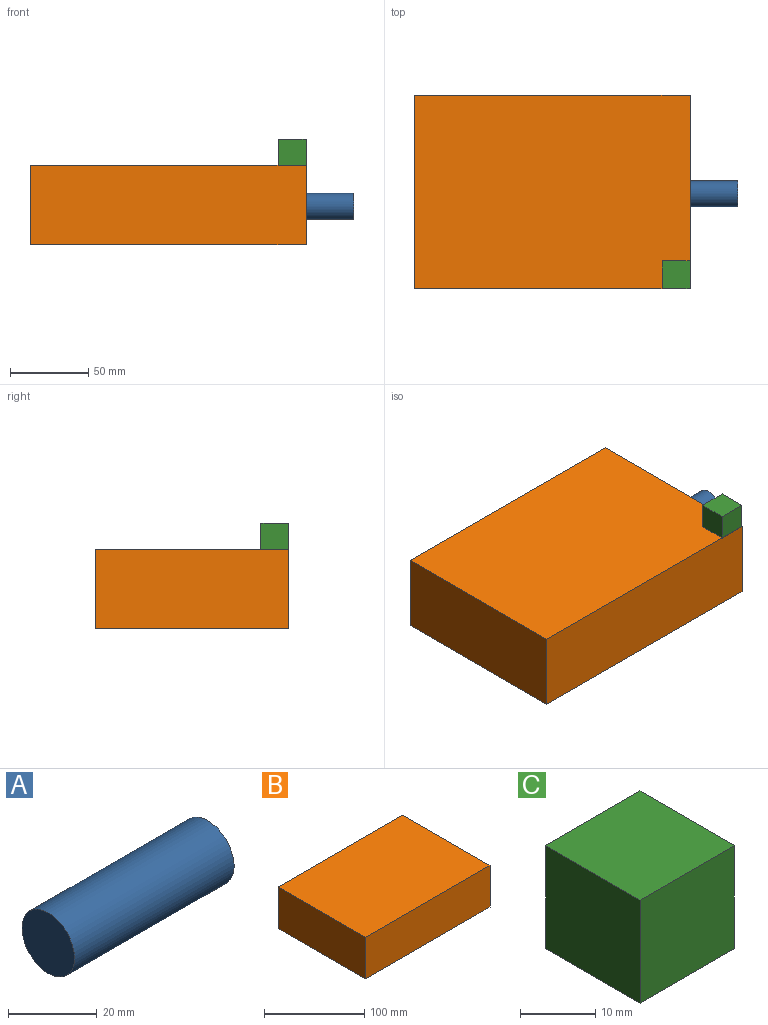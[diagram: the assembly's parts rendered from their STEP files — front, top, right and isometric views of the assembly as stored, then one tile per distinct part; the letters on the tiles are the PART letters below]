
ASSEMBLY  parts=3 mates=2
PART A: 3 faces, bbox 50.8x16.7x16.7 mm
  f0: cylinder r=8.35mm len=50.8mm, axis (-1,0,0), area 2665.5mm2, adj f1,f2
  f1: plane 16.7x16.7mm, normal (1,0,0), area 219.1mm2, adj f0
  f2: plane 16.7x16.7mm, normal (-1,0,0), area 219.1mm2, adj f0
PART B: 8 faces, bbox 176.1x123.5x50.8 mm
  f0: plane 123.51x50.8mm, normal (-1,0,0), area 6274.3mm2, adj f1,f3,f4,f5
  f1: plane 176.1x50.8mm, normal (0,-1,0), area 8945.8mm2, adj f0,f2,f4,f5
  f2: plane 123.51x50.8mm, normal (1,0,0), area 5196.8mm2, adj f1,f3,f4,f5,f6
  f3: plane 176.1x50.8mm, normal (0,1,0), area 8945.8mm2, adj f0,f2,f4,f5
  f4: plane 176.1x123.51mm, normal (0,0,1), area 21750mm2, adj f0,f1,f2,f3
  f5: plane 176.1x123.51mm, normal (0,0,-1), area 21750mm2, adj f0,f1,f2,f3
  f6: cylinder r=18.52mm len=37.04mm, axis (1,0,0), area 2364.5mm2, adj f2,f7
  f7: plane 37.04x37.04mm, normal (1,0,0), area 1077.5mm2, adj f6
PART C: 6 faces, bbox 17.8x17.8x16.8 mm
  f0: plane 17.78x16.76mm, normal (-1,0,0), area 298.1mm2, adj f1,f3,f4,f5
  f1: plane 17.78x16.76mm, normal (0,-1,0), area 298.1mm2, adj f0,f2,f4,f5
  f2: plane 17.78x16.76mm, normal (1,0,0), area 298.1mm2, adj f1,f3,f4,f5
  f3: plane 17.78x16.76mm, normal (0,1,0), area 298.1mm2, adj f0,f2,f4,f5
  f4: plane 17.78x17.78mm, normal (0,0,1), area 316.1mm2, adj f0,f1,f2,f3
  f5: plane 17.78x17.78mm, normal (0,0,-1), area 316.1mm2, adj f0,f1,f2,f3
PLACE A t=(47.28,31.78,-15.34)mm
PLACE B t=(5.8,-3.68,-11.26)mm
PLACE C t=(75.21,-76.46,39.54)mm
MATE fastened A.f0 <-> B.f6  axis (-1,0,0) through (47.28,-3.68,13.29)mm
MATE fastened C.f5 <-> B.f4  axis (0,0,1) through (67.6,-64.31,39.54)mm
